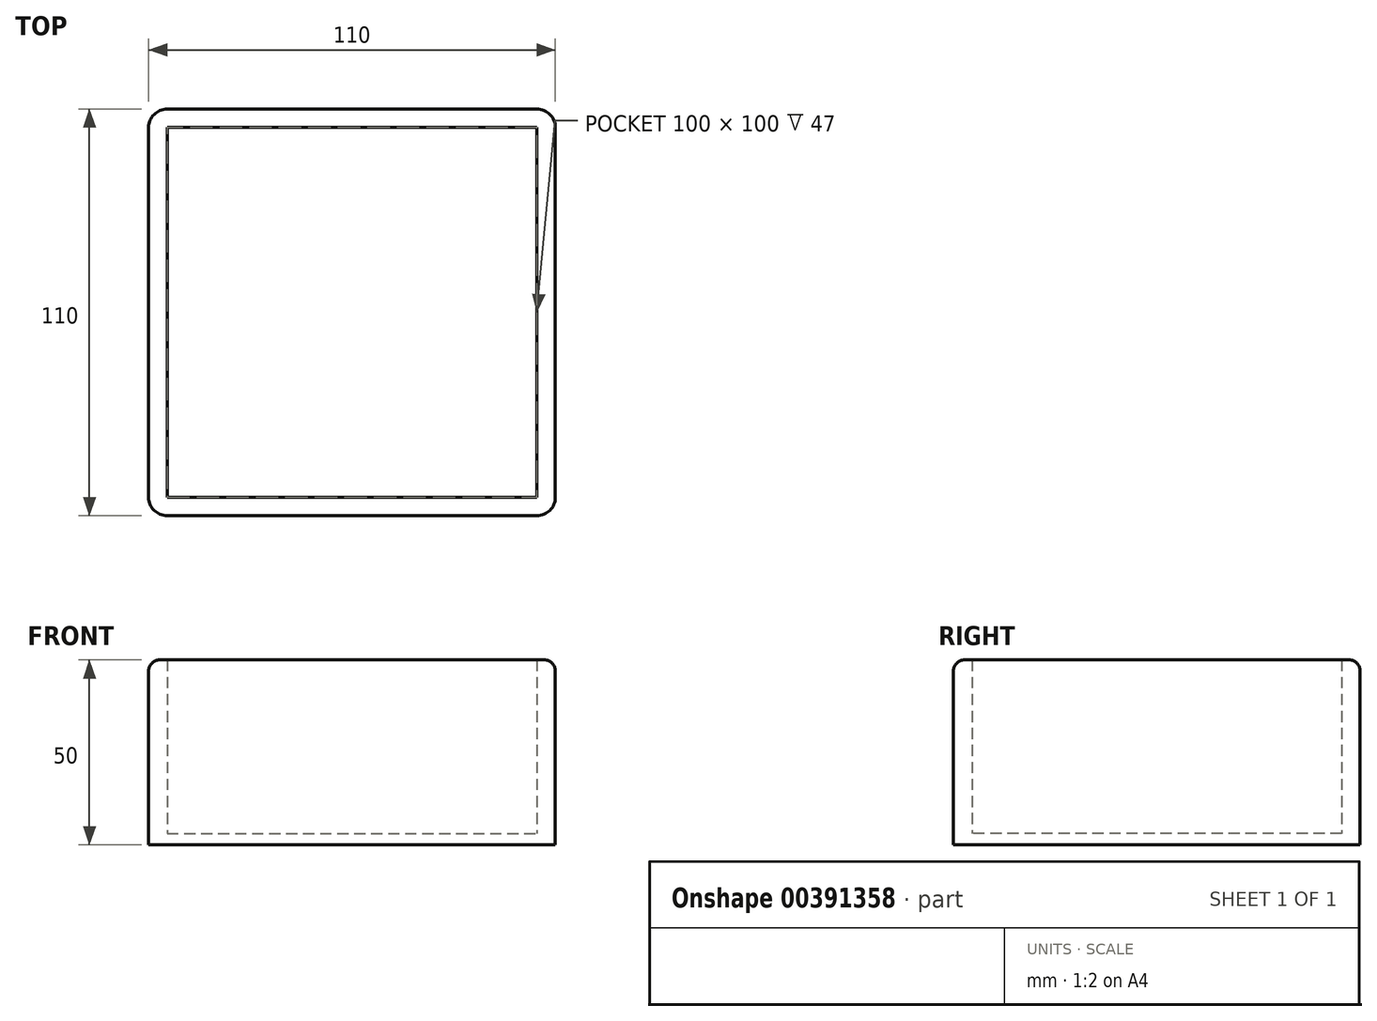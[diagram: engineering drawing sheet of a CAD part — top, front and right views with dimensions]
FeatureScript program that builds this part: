
annotation { "Feature Type Name" : "Feature", "Feature Type Description" : "" }
export const myFeature = defineFeature(function(context is Context, id is Id, definition is map)
    precondition{}
    {
        {
            var Q0;
            Q0=qCreatedBy(makeId("Top.planeOp"),FACE);
            var sketch = newSketch(context, id + "F0", { "sketchPlane" : qUnion([Q0])});
            skLineSegment(sketch, "E0.bottom", {"start": v(-46.5, 48.52) * mm, "end": v(53.5, 48.52) * mm});
            skLineSegment(sketch, "E0.top", {"start": v(-46.5, -51.48) * mm, "end": v(53.5, -51.48) * mm});
            skLineSegment(sketch, "E0.left", {"start": v(-46.5, 48.52) * mm, "end": v(-46.5, -51.48) * mm});
            skLineSegment(sketch, "E0.right", {"start": v(53.5, 48.52) * mm, "end": v(53.5, -51.48) * mm});
            skLineSegment(sketch, "E1.bottom", {"start": v(-46.5, 53.52) * mm, "end": v(53.5, 53.52) * mm});
            skLineSegment(sketch, "E1.top", {"start": v(-46.5, -56.48) * mm, "end": v(53.5, -56.48) * mm});
            skLineSegment(sketch, "E1.left", {"start": v(-51.5, 48.52) * mm, "end": v(-51.5, -51.48) * mm});
            skLineSegment(sketch, "E1.right", {"start": v(58.5, 48.52) * mm, "end": v(58.5, -51.48) * mm});
            skPoint(sketch, "E2.visualSharp", {"position": v(-51.5, 53.52) * mm});
            skArc(sketch, "E2.filletArc", {"start": v(-46.5, 53.52) * mm, "mid": v(-50.03, 52.06) * mm, "end": v(-51.5, 48.52) * mm});
            skPoint(sketch, "E3.visualSharp", {"position": v(58.5, 53.52) * mm});
            skArc(sketch, "E3.filletArc", {"start": v(58.5, 48.52) * mm, "mid": v(57.04, 52.06) * mm, "end": v(53.5, 53.52) * mm});
            skPoint(sketch, "E4.visualSharp", {"position": v(-51.5, -56.48) * mm});
            skArc(sketch, "E4.filletArc", {"start": v(-51.5, -51.48) * mm, "mid": v(-50.03, -55.01) * mm, "end": v(-46.5, -56.48) * mm});
            skPoint(sketch, "E5.visualSharp", {"position": v(58.5, -56.48) * mm});
            skArc(sketch, "E5.filletArc", {"start": v(53.5, -56.48) * mm, "mid": v(57.04, -55.01) * mm, "end": v(58.5, -51.48) * mm});
            skSolve(sketch);
        }
        {
            var Q0;
            Q0=makeQuery(id+"F0.imprint","IMPRINT",FACE,{"disambiguationData":[TD([[makeQuery(id+"F0.imprint","IMPRINT",EDGE,{"derivedFrom":sQuery(id+"F0.wireOp",EDGE,"E0.bottom")}),-1.0]])]});
            extrude(context, id + "F1", {"entities" : qUnion([Q0]), "depth" : 3 * mm});
        }
        {
            var Q0;
            Q0 = qSketchRegion(id + "F0", true);
            extrude(context, id + "F2", {"entities" : qUnion([Q0]), "operationType" : NewBodyOperationType.ADD, "depth" : 50 * mm});
        }
        {
            var Q0;
            Q0=makeQuery(id+"F2.opExtrude","CAP_EDGE",EDGE,{"disambiguationData":[OSD([sQuery(id+"F0.wireOp",EDGE,"E1.left")])],"isStart":false});
            fillet(context, id + "F3", {"entities" : qUnion([Q0]), "radius" : 3 * mm, "tangentPropagation" : true, "allowEdgeOverflow" : false});
        }
    });
